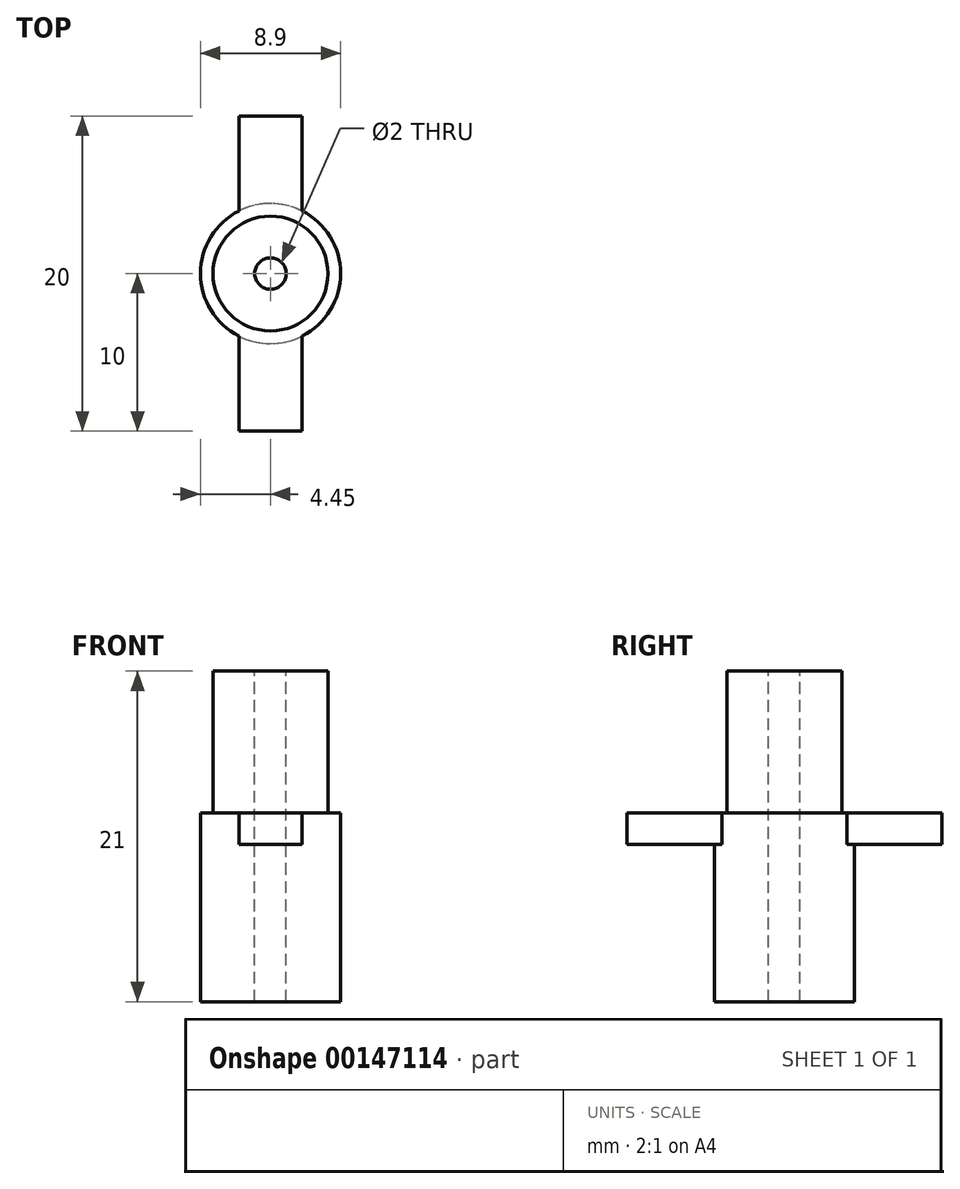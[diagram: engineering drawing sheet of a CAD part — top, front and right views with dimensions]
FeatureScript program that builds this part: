
annotation { "Feature Type Name" : "Feature", "Feature Type Description" : "" }
export const myFeature = defineFeature(function(context is Context, id is Id, definition is map)
    precondition{}
    {
        {
            var Q0;
            Q0=qCreatedBy(makeId("Top.planeOp"),FACE);
            var sketch = newSketch(context, id + "F0", { "sketchPlane" : qUnion([Q0])});
            skCircle(sketch, "E0", {"center": v(0, 0) * mm, "radius": 4.45 * mm});
            skCircle(sketch, "E1", {"center": v(0, 0) * mm, "radius": 1 * mm});
            skLineSegment(sketch, "E2.bottom", {"start": v(2, -10) * mm, "end": v(-2, -10) * mm});
            skLineSegment(sketch, "E2.top", {"start": v(2, 10) * mm, "end": v(-2, 10) * mm});
            skLineSegment(sketch, "E2.left", {"start": v(2, -10) * mm, "end": v(2, 10) * mm});
            skLineSegment(sketch, "E2.right", {"start": v(-2, -10) * mm, "end": v(-2, 10) * mm});
            skCircle(sketch, "E3", {"center": v(0, 0) * mm, "radius": 3.65 * mm});
            skSolve(sketch);
        }
        {
            var Q0;
            {var subQ0=sQuery(id+"F0.wireOp",EDGE,"E2.right");var subQ1=sQuery(id+"F0.wireOp",EDGE,"E0");var subQ2=makeQuery(id+"F0.imprint","INTERSECT",VERTEX,{"disambiguationData":[OD(0.0)],"derivedFrom":[subQ1,subQ0]});Q0=makeQuery(id+"F0.imprint","IMPRINT",FACE,{"disambiguationData":[TD([[makeQuery(id+"F0.imprint","IMPRINT",EDGE,{"disambiguationData":[TD([[subQ2,-1.0]])],"derivedFrom":subQ1}),1.0]])]});}
            var Q1;
            {var subQ0=sQuery(id+"F0.wireOp",EDGE,"E2.right");var subQ1=sQuery(id+"F0.wireOp",EDGE,"E0");var subQ2=makeQuery(id+"F0.imprint","INTERSECT",VERTEX,{"disambiguationData":[OD(1.0)],"derivedFrom":[subQ1,subQ0]});Q1=makeQuery(id+"F0.imprint","IMPRINT",FACE,{"disambiguationData":[TD([[makeQuery(id+"F0.imprint","IMPRINT",EDGE,{"disambiguationData":[TD([[subQ2,-1.0]])],"derivedFrom":subQ1}),1.0]])]});}
            var Q2;
            {var subQ0=sQuery(id+"F0.wireOp",EDGE,"E2.left");var subQ1=sQuery(id+"F0.wireOp",EDGE,"E0");var subQ2=makeQuery(id+"F0.imprint","INTERSECT",VERTEX,{"disambiguationData":[OD(0.0)],"derivedFrom":[subQ1,subQ0]});Q2=makeQuery(id+"F0.imprint","IMPRINT",FACE,{"disambiguationData":[TD([[makeQuery(id+"F0.imprint","IMPRINT",EDGE,{"disambiguationData":[TD([[subQ2,1.0]])],"derivedFrom":subQ1}),1.0]])]});}
            var Q3;
            {var subQ0=sQuery(id+"F0.wireOp",EDGE,"E2.right");var subQ1=sQuery(id+"F0.wireOp",EDGE,"E0");var subQ2=makeQuery(id+"F0.imprint","INTERSECT",VERTEX,{"disambiguationData":[OD(0.0)],"derivedFrom":[subQ1,subQ0]});Q3=makeQuery(id+"F0.imprint","IMPRINT",FACE,{"disambiguationData":[TD([[makeQuery(id+"F0.imprint","IMPRINT",EDGE,{"disambiguationData":[TD([[subQ2,1.0]])],"derivedFrom":subQ1}),1.0]])]});}
            var Q4;
            {var subQ0=sQuery(id+"F0.wireOp",EDGE,"E3");var subQ1=sQuery(id+"F0.wireOp",EDGE,"E2.right");var subQ2=makeQuery(id+"F0.imprint","INTERSECT",VERTEX,{"disambiguationData":[OD(0.0)],"derivedFrom":[subQ1,subQ0]});Q4=makeQuery(id+"F0.imprint","IMPRINT",FACE,{"disambiguationData":[TD([[makeQuery(id+"F0.imprint","IMPRINT",EDGE,{"disambiguationData":[TD([[subQ2,-1.0]])],"derivedFrom":subQ1}),1.0]])]});}
            var Q5;
            Q5=makeQuery(id+"F0.imprint","IMPRINT",FACE,{"disambiguationData":[TD([[makeQuery(id+"F0.imprint","IMPRINT",EDGE,{"derivedFrom":sQuery(id+"F0.wireOp",EDGE,"E1")}),-1.0]])]});
            var Q6;
            {var subQ0=sQuery(id+"F0.wireOp",EDGE,"E3");var subQ1=sQuery(id+"F0.wireOp",EDGE,"E2.left");var subQ2=makeQuery(id+"F0.imprint","INTERSECT",VERTEX,{"disambiguationData":[OD(0.0)],"derivedFrom":[subQ1,subQ0]});Q6=makeQuery(id+"F0.imprint","IMPRINT",FACE,{"disambiguationData":[TD([[makeQuery(id+"F0.imprint","IMPRINT",EDGE,{"disambiguationData":[TD([[subQ2,-1.0]])],"derivedFrom":subQ1}),-1.0]])]});}
            extrude(context, id + "F1", {"entities" : qUnion([Q0, Q1, Q2, Q3, Q4, Q5, Q6]), "oppositeDirection" : true, "depth" : 11 * mm});
        }
        {
            var Q0;
            {var subQ5=sQuery(id+"F0.wireOp",EDGE,"E2.top");Q0=makeQuery(id+"F0.imprint","IMPRINT",FACE,{"disambiguationData":[TD([[makeQuery(id+"F0.imprint","IMPRINT",EDGE,{"derivedFrom":subQ5}),1.0]])]});}
            var Q1;
            {var subQ5=sQuery(id+"F0.wireOp",EDGE,"E2.bottom");Q1=makeQuery(id+"F0.imprint","IMPRINT",FACE,{"disambiguationData":[TD([[makeQuery(id+"F0.imprint","IMPRINT",EDGE,{"derivedFrom":subQ5}),-1.0]])]});}
            var Q2;
            {var subQ0=sQuery(id+"F0.wireOp",EDGE,"E2.right");var subQ1=sQuery(id+"F0.wireOp",EDGE,"E0");var subQ2=makeQuery(id+"F0.imprint","INTERSECT",VERTEX,{"disambiguationData":[OD(0.0)],"derivedFrom":[subQ1,subQ0]});Q2=makeQuery(id+"F0.imprint","IMPRINT",FACE,{"disambiguationData":[TD([[makeQuery(id+"F0.imprint","IMPRINT",EDGE,{"disambiguationData":[TD([[subQ2,1.0]])],"derivedFrom":subQ1}),1.0]])]});}
            var Q3;
            {var subQ0=sQuery(id+"F0.wireOp",EDGE,"E2.right");var subQ1=sQuery(id+"F0.wireOp",EDGE,"E0");var subQ2=makeQuery(id+"F0.imprint","INTERSECT",VERTEX,{"disambiguationData":[OD(1.0)],"derivedFrom":[subQ1,subQ0]});Q3=makeQuery(id+"F0.imprint","IMPRINT",FACE,{"disambiguationData":[TD([[makeQuery(id+"F0.imprint","IMPRINT",EDGE,{"disambiguationData":[TD([[subQ2,-1.0]])],"derivedFrom":subQ1}),1.0]])]});}
            var Q4;
            {var subQ0=sQuery(id+"F0.wireOp",EDGE,"E2.right");var subQ1=sQuery(id+"F0.wireOp",EDGE,"E0");var subQ2=makeQuery(id+"F0.imprint","INTERSECT",VERTEX,{"disambiguationData":[OD(0.0)],"derivedFrom":[subQ1,subQ0]});Q4=makeQuery(id+"F0.imprint","IMPRINT",FACE,{"disambiguationData":[TD([[makeQuery(id+"F0.imprint","IMPRINT",EDGE,{"disambiguationData":[TD([[subQ2,-1.0]])],"derivedFrom":subQ1}),1.0]])]});}
            var Q5;
            {var subQ0=sQuery(id+"F0.wireOp",EDGE,"E2.left");var subQ1=sQuery(id+"F0.wireOp",EDGE,"E0");var subQ2=makeQuery(id+"F0.imprint","INTERSECT",VERTEX,{"disambiguationData":[OD(0.0)],"derivedFrom":[subQ1,subQ0]});Q5=makeQuery(id+"F0.imprint","IMPRINT",FACE,{"disambiguationData":[TD([[makeQuery(id+"F0.imprint","IMPRINT",EDGE,{"disambiguationData":[TD([[subQ2,1.0]])],"derivedFrom":subQ1}),1.0]])]});}
            extrude(context, id + "F2", {"entities" : qUnion([Q0, Q1, Q2, Q3, Q4, Q5]), "operationType" : NewBodyOperationType.ADD, "endBound" : BoundingType.SYMMETRIC, "depth" : 2 * mm});
        }
        {
            var Q0;
            {var subQ0=sQuery(id+"F0.wireOp",EDGE,"E3");var subQ1=sQuery(id+"F0.wireOp",EDGE,"E2.right");var subQ2=makeQuery(id+"F0.imprint","INTERSECT",VERTEX,{"disambiguationData":[OD(0.0)],"derivedFrom":[subQ1,subQ0]});Q0=makeQuery(id+"F0.imprint","IMPRINT",FACE,{"disambiguationData":[TD([[makeQuery(id+"F0.imprint","IMPRINT",EDGE,{"disambiguationData":[TD([[subQ2,-1.0]])],"derivedFrom":subQ1}),1.0]])]});}
            var Q1;
            Q1=makeQuery(id+"F0.imprint","IMPRINT",FACE,{"disambiguationData":[TD([[makeQuery(id+"F0.imprint","IMPRINT",EDGE,{"derivedFrom":sQuery(id+"F0.wireOp",EDGE,"E1")}),-1.0]])]});
            var Q2;
            {var subQ0=sQuery(id+"F0.wireOp",EDGE,"E3");var subQ1=sQuery(id+"F0.wireOp",EDGE,"E2.left");var subQ2=makeQuery(id+"F0.imprint","INTERSECT",VERTEX,{"disambiguationData":[OD(0.0)],"derivedFrom":[subQ1,subQ0]});Q2=makeQuery(id+"F0.imprint","IMPRINT",FACE,{"disambiguationData":[TD([[makeQuery(id+"F0.imprint","IMPRINT",EDGE,{"disambiguationData":[TD([[subQ2,-1.0]])],"derivedFrom":subQ1}),-1.0]])]});}
            extrude(context, id + "F3", {"entities" : qUnion([Q0, Q1, Q2]), "operationType" : NewBodyOperationType.ADD, "depth" : 10 * mm});
        }
    });
